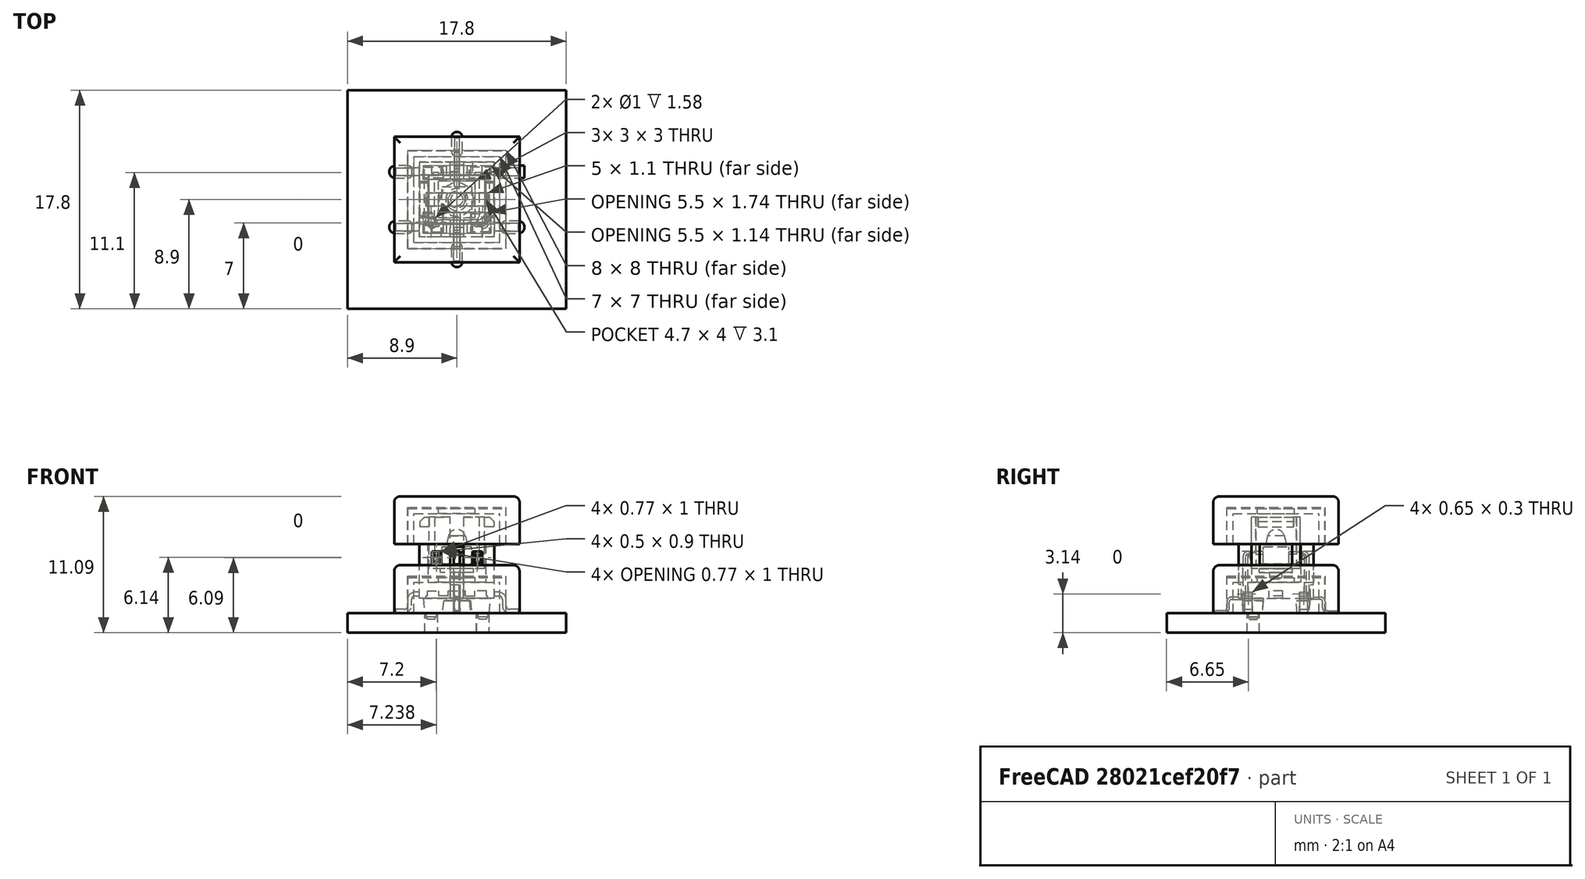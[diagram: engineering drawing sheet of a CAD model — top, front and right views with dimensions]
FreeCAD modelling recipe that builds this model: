
FCSTD DOCUMENT  (FreeCAD 0.17R13541 (Git))
Label: TL3240F160x_TL3240S1CAP
License: All rights reserved
LicenseURL: http://en.wikipedia.org/wiki/All_rights_reserved
objects: Part::FeaturePython×5, Part::Feature×5, Part::Box×5, Part::Cut×2, App::Part×2, App::DocumentObjectGroup×1, Part::Fillet×1, Part::Fuse×1
note: 19 computed .brp shape members not serialized (recipe doc carries the construction recipe); baked Part::Feature solids carry a one-line shape summary decoded from their .brp

FEATURE [Part::FeaturePython] FCrtYd_lines  label="FCrtYd"  # a2plus imported part (geometry in sourceFile) (typed FeaturePython)
  fixedPosition = true
FEATURE [Part::FeaturePython] Filk_lines  label="FrontSilk"  # a2plus imported part (geometry in sourceFile) (typed FeaturePython)
  fixedPosition = true
FEATURE [Part::FeaturePython] TopPads  # a2plus imported part (geometry in sourceFile) (typed FeaturePython)
  fixedPosition = true
FEATURE [Part::FeaturePython] THPs  label="PTHs"  # a2plus imported part (geometry in sourceFile) (typed FeaturePython)
  fixedPosition = true
FEATURE [Part::FeaturePython] newPCB  label="Pcb"  # a2plus imported part (geometry in sourceFile) (typed FeaturePython)
  fixedPosition = true
FEATURE [App::DocumentObjectGroup] E_Switch_SPST_LED_SquareCap_TL3240F160x_fp
  Group = -> [FCrtYd_lines,Filk_lines,TopPads,THPs,newPCB]
FEATURE [Part::Feature] Part__Feature  label="TL3240xxxx"
  Placement = pos=(0,0,1) rot=(0,0,1;3.14159rad)
  shape: bbox 10.01 x 10.01 x 8.308 mm, 263 faces (baked)
FEATURE [Part::Box] Box  label="Cube"
  AttacherType = Attacher::AttachEngine3D
  Height = 3.9
  Length = 10.2
  Placement = pos=(-5.1,-5.1,0) rot=(0,0,1;0rad)
  Width = 10.2
FEATURE [Part::Box] Box004  label="Cube004"
  AttacherType = Attacher::AttachEngine3D
  Height = 4
  Length = 3
  Placement = pos=(-1.5,-1.5,0) rot=(0,0,1;0rad)
  Width = 3
FEATURE [Part::Box] Box002  label="Cube002"
  AttacherType = Attacher::AttachEngine3D
  Height = 2.9
  Length = 7.96
  Placement = pos=(-3.98,-3.98,0) rot=(0,0,1;0rad)
  Width = 7.96
FEATURE [Part::Box] Box001  label="Cube001"
  AttacherType = Attacher::AttachEngine3D
  Height = 3
  Length = 8
  Placement = pos=(-4,-4,0) rot=(0,0,1;0rad)
  Width = 8
FEATURE [Part::Box] Box003  label="Cube003"
  AttacherType = Attacher::AttachEngine3D
  Height = 2.5
  Length = 7
  Placement = pos=(-3.5,-3.5,0) rot=(0,0,1;0rad)
  Width = 7
FEATURE [Part::Cut] Cut
  Base = -> Box
  Tool = -> Box001
FEATURE [Part::Fillet] Fillet
  Base = -> Cut
  Edges = 4 edges r=0.5: [Edge2,Edge7,Edge8,Edge9]
FEATURE [Part::Fuse] Fusion
  Base = -> Box003
  Tool = -> Box004
FEATURE [Part::Cut] Cut001
  Base = -> Box002
  Tool = -> Fusion
FEATURE [App::Part] Part002  label="TL3240S1CAP"
  Group = -> [Cut,Box001,Box,Fillet,Fusion,Box003,Box004,Box002,Cut001]
  License = CC BY 3.0
  LicenseURL = http://creativecommons.org/licenses/by/3.0/
  Origin = -> Origin002
  Placement = pos=(0,0,5.6) rot=(0,0,1;0rad)
FEATURE [App::Part] Part001  label="TL3240xxxx_TL3240S1CAP"
  Group = -> [Part__Feature,Part002]
  License = CC BY 3.0
  LicenseURL = http://creativecommons.org/licenses/by/3.0/
  Origin = -> Origin001
FEATURE [Part::Feature] Part__Feature_cp  label="TL3240xxxx_cp"
  Placement = pos=(0,0,1) rot=(0,0,1;3.14159rad)
  shape: bbox 10.01 x 10.01 x 8.308 mm, 263 faces (baked)
FEATURE [Part::Feature] Fillet_cp
  Placement = pos=(0,0,5.6) rot=(0,0,1;0rad)
  shape: bbox 10.2 x 10.2 x 3.9 mm, 15 faces (baked)
FEATURE [Part::Feature] Cut001_cp
  Placement = pos=(0,0,5.6) rot=(0,0,1;0rad)
  shape: bbox 7.96 x 7.96 x 2.9 mm, 15 faces (baked)
FEATURE [Part::Feature] Shape  label="TL3240xxxx_TL3240S1CAP_cp"
  shape: bbox 10.21 x 10.21 x 10.01 mm, 293 faces, 3 solids (baked)
